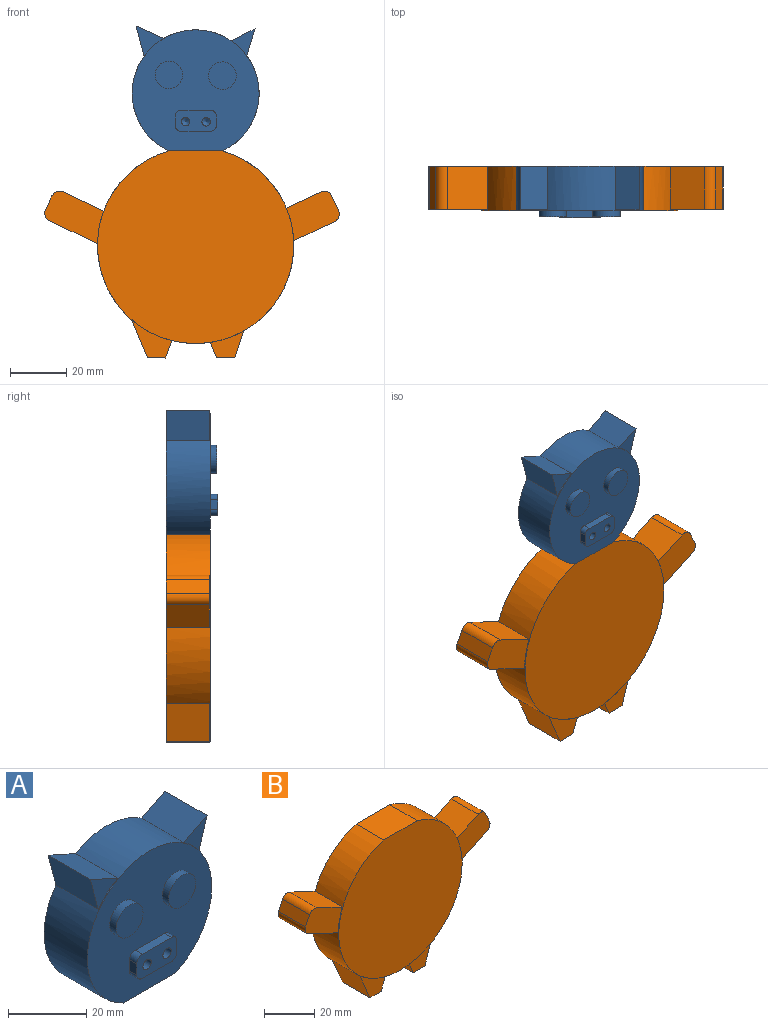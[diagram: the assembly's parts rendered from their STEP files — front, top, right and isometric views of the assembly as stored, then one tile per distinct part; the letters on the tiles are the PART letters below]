
ASSEMBLY  parts=2 mates=1
PART A: 27 faces, bbox 45x18.2x44.3 mm
  f0: plane 44.99x42.9mm, normal (0,-1,0), area 1307.8mm2, adj f1,f2,f10,f12,f14,f15,f16,f17
  f1: plane 18.92x15.6mm, normal (0,0,-1), area 295.2mm2, adj f0,f2,f3
  f2: cylinder r=22.49mm len=44.99mm, axis (0,1,0), area 1636.3mm2, adj f0,f1,f3,f4,f5,f6,f7,f8
  f3: plane 44.99x44.27mm, normal (0,1,0), area 1639.1mm2, adj f1,f2,f4,f5,f7,f8
  f4: plane 15.3x10.7mm, normal (-0.97,0,-0.26), area 169.4mm2, adj f2,f3,f5,f6
  f5: plane 15.3x9.82mm, normal (0.41,0,0.91), area 164.6mm2, adj f2,f3,f4,f6
  f6: plane 10.7x9.82mm, normal (0,-1,0), area 43.2mm2, adj f2,f4,f5
  f7: plane 15.3x8.5mm, normal (-0.45,0,0.89), area 145.4mm2, adj f2,f3,f8,f9
  f8: plane 15.3x9.6mm, normal (0.96,0,-0.29), area 153.7mm2, adj f2,f3,f7,f9
  f9: plane 9.6x8.5mm, normal (0,-1,0), area 32.9mm2, adj f2,f7,f8
  f10: cylinder r=4.88mm len=9.76mm, axis (0,1,0), area 70.1mm2, adj f0,f11
  f11: plane 9.76x9.76mm, normal (0,-1,0), area 74.8mm2, adj f10
  f12: cylinder r=4.88mm len=9.76mm, axis (0,1,0), area 70.1mm2, adj f0,f13
  f13: plane 9.76x9.76mm, normal (0,-1,0), area 74.8mm2, adj f12
  f14: cylinder r=2mm len=2.6mm, axis (0,1,0), area 8.2mm2, adj f0,f15,f21,f22
  f15: plane 10.56x2.6mm, normal (0,0,-1), area 27.4mm2, adj f0,f14,f16,f22
  f16: cylinder r=2mm len=2.6mm, axis (0,1,0), area 8.2mm2, adj f0,f15,f17,f22
  f17: plane 3.49x2.6mm, normal (1,0,0), area 9.1mm2, adj f0,f16,f18,f22
  f18: cylinder r=2mm len=2.6mm, axis (0,1,0), area 8.2mm2, adj f0,f17,f19,f22
  f19: plane 10.56x2.6mm, normal (0,0,1), area 27.4mm2, adj f0,f18,f20,f22
  f20: cylinder r=2mm len=2.6mm, axis (0,1,0), area 8.2mm2, adj f0,f19,f21,f22
  f21: plane 3.49x2.6mm, normal (-1,0,0), area 9.1mm2, adj f0,f14,f20,f22
  f22: plane 14.56x7.49mm, normal (0,-1,0), area 91.5mm2, adj f14,f15,f16,f17,f18,f19,f20,f21
  f23: cone r=0mm half-angle=59deg, axis (0,-1,0), area 8.2mm2, adj f24
  f24: cylinder r=1.5mm len=7mm, axis (0,-1,0), area 66mm2, adj f22,f23
  f25: cone r=0mm half-angle=59deg, axis (0,-1,0), area 8.2mm2, adj f26
  f26: cylinder r=1.5mm len=7mm, axis (0,-1,0), area 66mm2, adj f22,f25
PART B: 25 faces, bbox 104.4x15.6x73.4 mm
  f0: cylinder r=34.79mm len=69.58mm, axis (0,1,0), area 2307.6mm2, adj f1,f2,f3,f4,f5,f9,f10,f11
  f1: plane 18.92x15.6mm, normal (0,0,1), area 295.1mm2, adj f0,f2,f3
  f2: plane 69.58x68.27mm, normal (0,-1,0), area 3785.7mm2, adj f0,f1
  f3: plane 104.4x73.39mm, normal (0,1,0), area 4353.4mm2, adj f0,f1,f4,f5,f6,f7,f8,f10
  f4: plane 15.3x14.31mm, normal (0.43,0,0.9), area 242.4mm2, adj f0,f3,f6,f9
  f5: plane 16.99x15.3mm, normal (-0.43,0,-0.9), area 287.8mm2, adj f0,f3,f8,f9
  f6: cylinder r=3mm len=15.3mm, axis (0,1,0), area 72.1mm2, adj f3,f4,f7,f9
  f7: plane 15.3x4.82mm, normal (-0.9,0,0.43), area 81.7mm2, adj f3,f6,f8,f9
  f8: cylinder r=3mm len=15.3mm, axis (0,1,0), area 72.1mm2, adj f3,f5,f7,f9
  f9: plane 20.89x18.6mm, normal (0,-1,0), area 222.8mm2, adj f0,f4,f5,f6,f7,f8
  f10: plane 15.2x12.08mm, normal (-0.42,0,0.91), area 202.8mm2, adj f0,f3,f14,f15
  f11: plane 15.2x14.43mm, normal (0.42,0,-0.91), area 242.3mm2, adj f0,f3,f12,f15
  f12: cylinder r=3mm len=15.2mm, axis (0,1,0), area 71.6mm2, adj f3,f11,f13,f15
  f13: plane 15.2x5.06mm, normal (0.91,0,0.42), area 84.9mm2, adj f3,f12,f14,f15
  f14: cylinder r=3mm len=15.2mm, axis (0,1,0), area 71.6mm2, adj f3,f10,f13,f15
  f15: plane 18.73x17.55mm, normal (0,-1,0), area 196.5mm2, adj f0,f10,f11,f12,f13,f14
  f16: plane 15.4x13.58mm, normal (-0.92,0,-0.39), area 227mm2, adj f0,f3,f18,f20
  f17: plane 15.4x0.27mm, normal (0.5,0,0.86), area 4.7mm2, adj f0,f3,f19,f20
  f18: plane 15.4x6.4mm, normal (-0.01,0,-1), area 98.5mm2, adj f3,f16,f19,f20
  f19: plane 15.4x6.07mm, normal (0.94,0,-0.35), area 99.6mm2, adj f3,f17,f18,f20
  f20: plane 14.38x13.63mm, normal (0,-1,0), area 85.6mm2, adj f0,f16,f17,f18,f19
  f21: plane 15.5x5.46mm, normal (-0.93,0,-0.38), area 91.4mm2, adj f0,f3,f23,f24
  f22: plane 15.5x9.5mm, normal (0.95,0,-0.31), area 154.8mm2, adj f0,f3,f23,f24
  f23: plane 15.5x6.48mm, normal (0,0,-1), area 100.4mm2, adj f3,f21,f22,f24
  f24: plane 11.8x9.5mm, normal (0,-1,0), area 62.8mm2, adj f0,f21,f22,f23
PLACE A t=(-13.75,-27.69,-1.97)mm
PLACE B t=(-13.74,-27.69,-2.59)mm fixed
MATE fastened B.f1 <-> A.f1  axis (0,0,1) through (-4.29,-43.29,-4.18)mm
